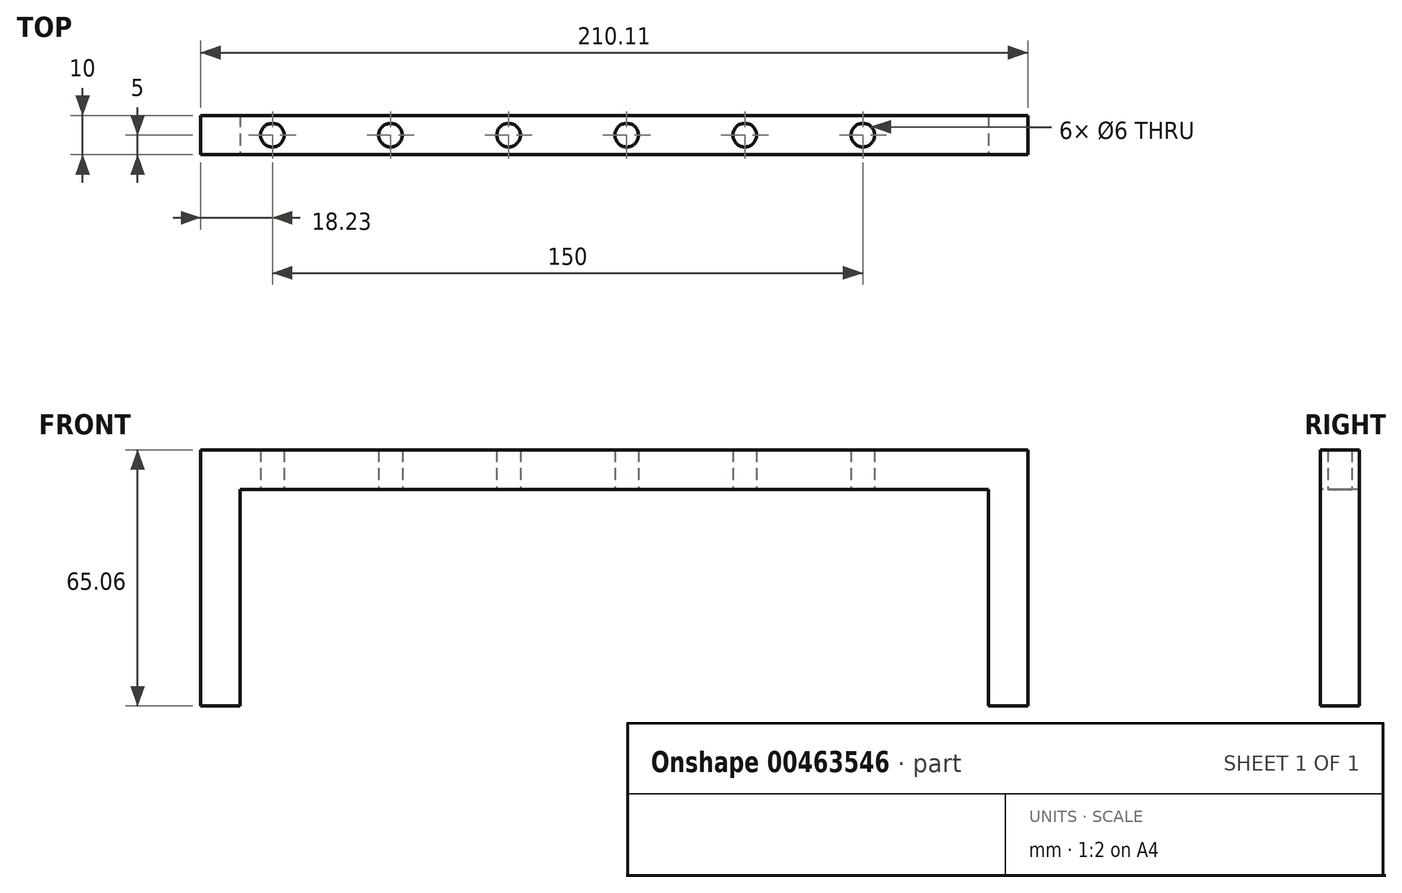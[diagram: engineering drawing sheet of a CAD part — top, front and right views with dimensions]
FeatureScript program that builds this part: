
annotation { "Feature Type Name" : "Feature", "Feature Type Description" : "" }
export const myFeature = defineFeature(function(context is Context, id is Id, definition is map)
    precondition{}
    {
        {
            var Q0;
            Q0=qCreatedBy(makeId("Front.planeOp"),FACE);
            var sketch = newSketch(context, id + "F0", { "sketchPlane" : qUnion([Q0])});
            skLineSegment(sketch, "E0", {"start": v(-59.48, 0) * mm, "end": v(-59.48, 60) * mm});
            skLineSegment(sketch, "E1", {"start": v(-59.48, 60) * mm, "end": v(140.52, 60) * mm});
            skLineSegment(sketch, "E2", {"start": v(140.52, 60) * mm, "end": v(140.52, 0) * mm});
            skSolve(sketch);
        }
        {
            var Q0;
            Q0=qCreatedBy(makeId("Top.planeOp"),FACE);
            var sketch = newSketch(context, id + "F1", { "sketchPlane" : qUnion([Q0])});
            skLineSegment(sketch, "E3.bottom", {"start": v(-54.54, 5) * mm, "end": v(-64.54, 5) * mm});
            skLineSegment(sketch, "E3.top", {"start": v(-54.54, -5) * mm, "end": v(-64.54, -5) * mm});
            skLineSegment(sketch, "E3.left", {"start": v(-54.54, 5) * mm, "end": v(-54.54, -5) * mm});
            skLineSegment(sketch, "E3.right", {"start": v(-64.54, 5) * mm, "end": v(-64.54, -5) * mm});
            skPoint(sketch, "E3.middle", {"position": v(-59.54, 0) * mm});
            skSolve(sketch);
        }
        {
            var Q0;
            Q0=makeQuery(id+"F1.imprint","IMPRINT",FACE,{"disambiguationData":[TD([[makeQuery(id+"F1.imprint","IMPRINT",EDGE,{"derivedFrom":sQuery(id+"F1.wireOp",EDGE,"E3.bottom")}),1.0]])]});
            var Q1;
            Q1 = qConstructionFilter(qBodyType(qCreatedBy(id + "F0" ,EDGE), BodyType.WIRE), ConstructionObject.NO);
            sweep(context, id + "F2", {"profiles" : qUnion([Q0]), "path" : qUnion([Q1])});
        }
        {
            var Q0;
            Q0=makeQuery(id+"F2.opSweep","SWEPT_FACE",FACE,{"disambiguationData":[OSD([sQuery(id+"F0.wireOp",EDGE,"E1"),sQuery(id+"F1.wireOp",EDGE,"E3.left")])]});
            var sketch = newSketch(context, id + "F3", { "sketchPlane" : qUnion([Q0])});
            skLineSegment(sketch, "E4", {"start": v(-70.97, 0) * mm, "end": v(148.4, 0) * mm});
            skCircle(sketch, "E5", {"center": v(-46.31, 0) * mm, "radius": 3 * mm});
            skCircle(sketch, "E6.1.0.0", {"center": v(-16.31, 0) * mm, "radius": 3 * mm});
            skCircle(sketch, "E6.2.0.0", {"center": v(13.69, 0) * mm, "radius": 3 * mm});
            skCircle(sketch, "E6.3.0.0", {"center": v(43.69, 0) * mm, "radius": 3 * mm});
            skCircle(sketch, "E6.4.0.0", {"center": v(73.69, 0) * mm, "radius": 3 * mm});
            skCircle(sketch, "E6.5.0.0", {"center": v(103.69, 0) * mm, "radius": 3 * mm});
            skLineSegment(sketch, "E6.direction1", {"start": v(-46.31, 0) * mm, "end": v(-16.31, 0) * mm, "construction": true});
            skSolve(sketch);
        }
        {
            var Q0;
            Q0 = qSketchRegion(id + "F3", true);
            extrude(context, id + "F4", {"entities" : qUnion([Q0]), "operationType" : NewBodyOperationType.REMOVE, "oppositeDirection" : true, "depth" : 25 * mm, "offsetDistance" : 25 * mm});
        }
    });
